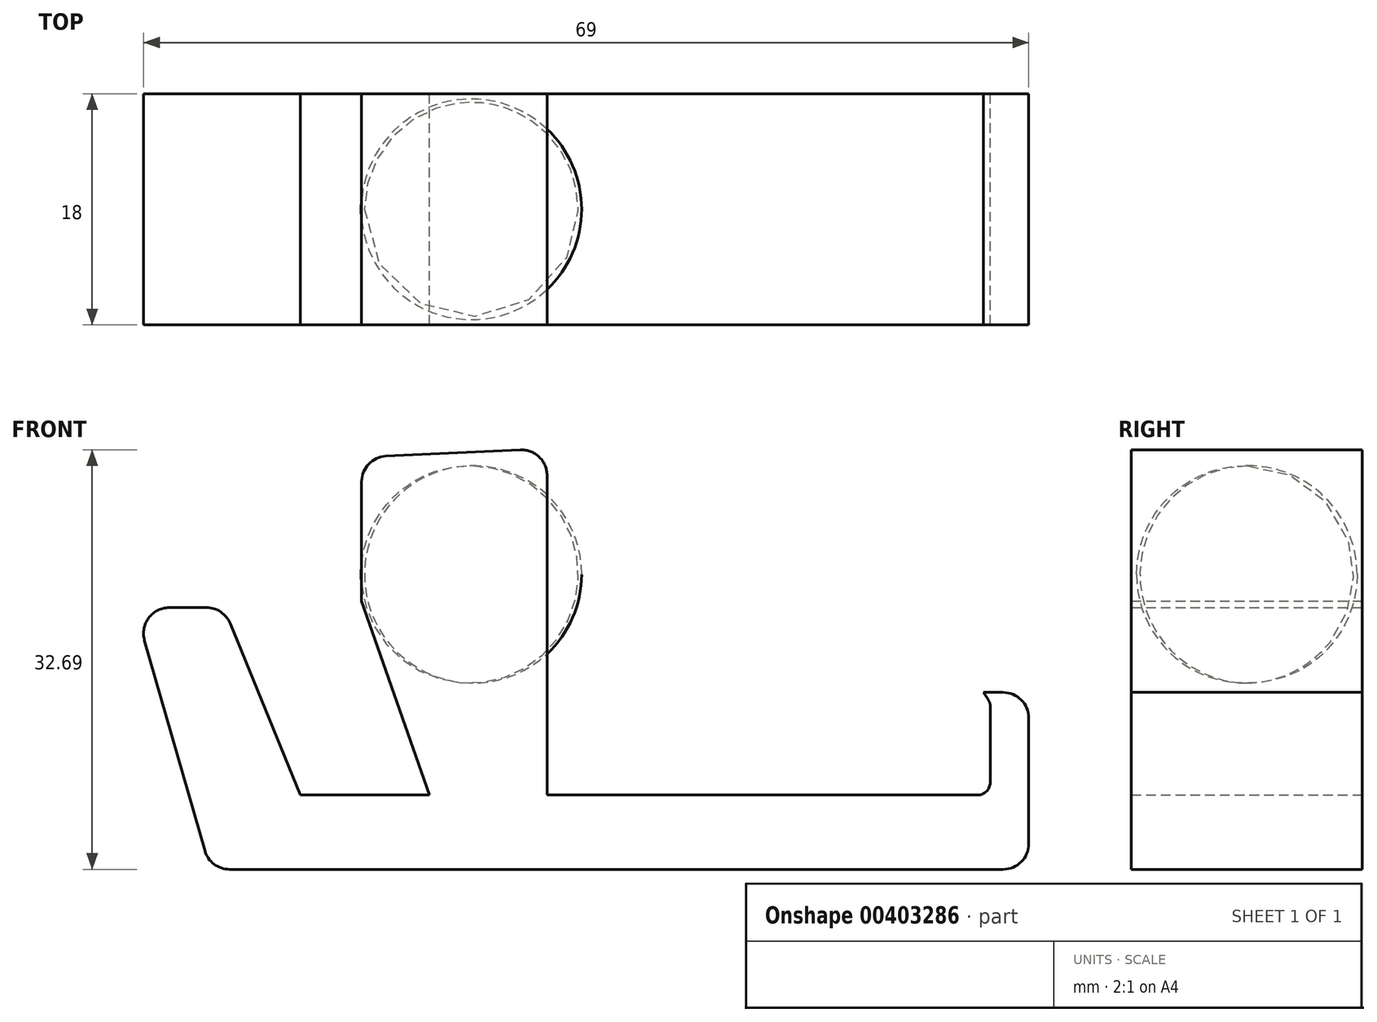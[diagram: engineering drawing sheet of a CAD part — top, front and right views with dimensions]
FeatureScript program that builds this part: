
annotation { "Feature Type Name" : "Feature", "Feature Type Description" : "" }
export const myFeature = defineFeature(function(context is Context, id is Id, definition is map)
    precondition{}
    {
        {
            var Q0;
            Q0=qCreatedBy(makeId("Front.planeOp"),FACE);
            var sketch = newSketch(context, id + "F0", { "sketchPlane" : qUnion([Q0])});
            skLineSegment(sketch, "E0", {"start": v(14.6, 13.8) * mm, "end": v(14.6, 0) * mm});
            skLineSegment(sketch, "E1", {"start": v(14.6, 0) * mm, "end": v(-21.99, 0) * mm});
            skLineSegment(sketch, "E2", {"start": v(-21.99, 0) * mm, "end": v(-49.2, 0) * mm});
            skLineSegment(sketch, "E3", {"start": v(-49.2, 0) * mm, "end": v(-55.06, 20.4) * mm});
            skLineSegment(sketch, "E4", {"start": v(-55.06, 20.4) * mm, "end": v(-48.16, 20.4) * mm});
            skLineSegment(sketch, "E5", {"start": v(-48.16, 20.4) * mm, "end": v(-42.19, 5.8) * mm});
            skLineSegment(sketch, "E6", {"start": v(-42.19, 5.8) * mm, "end": v(-32.13, 5.8) * mm});
            skLineSegment(sketch, "E7", {"start": v(-32.13, 5.8) * mm, "end": v(-37.4, 20.92) * mm});
            skLineSegment(sketch, "E8", {"start": v(-37.4, 20.92) * mm, "end": v(-37.4, 32.12) * mm});
            skLineSegment(sketch, "E9", {"start": v(-37.4, 32.12) * mm, "end": v(-22.95, 32.8) * mm});
            skLineSegment(sketch, "E10", {"start": v(-21.99, 0) * mm, "end": v(-21.99, 0) * mm});
            skLineSegment(sketch, "E11", {"start": v(-22.95, 5.8) * mm, "end": v(11.6, 5.8) * mm});
            skLineSegment(sketch, "E12", {"start": v(11.6, 5.8) * mm, "end": v(11.6, 13) * mm});
            skLineSegment(sketch, "E13", {"start": v(-22.95, 32.8) * mm, "end": v(-22.95, 5.8) * mm});
            skLineSegment(sketch, "E14", {"start": v(11.6, 13) * mm, "end": v(11.07, 13.8) * mm});
            skLineSegment(sketch, "E15", {"start": v(11.07, 13.8) * mm, "end": v(14.6, 13.8) * mm});
            skSolve(sketch);
        }
        {
            var Q0;
            Q0=makeQuery(id+"F0.imprint","IMPRINT",FACE,{"disambiguationData":[TD([[makeQuery(id+"F0.imprint","IMPRINT",EDGE,{"derivedFrom":sQuery(id+"F0.wireOp",EDGE,"E0")}),-1.0]])]});
            extrude(context, id + "F1", {"entities" : qUnion([Q0]), "depth" : 18 * mm});
        }
        {
            var Q0;
            Q0=makeQuery(id+"F1.opExtrude","SWEPT_EDGE",EDGE,{"disambiguationData":[OSD([sQuery(id+"F0.wireOp",EDGE,"E12"),sQuery(id+"F0.wireOp",EDGE,"p1Uv713Y-vDOA-6ysD-XTqa-nBpN6AyQfED6")])]});
            fillet(context, id + "F2", {"entities" : qUnion([Q0]), "radius" : 1 * mm, "tangentPropagation" : true, "allowEdgeOverflow" : false});
        }
        {
            var Q0;
            Q0=makeQuery(id+"F1.opExtrude","SWEPT_FACE",FACE,{"disambiguationData":[OSD([sQuery(id+"F0.wireOp",EDGE,"E13")])]});
            var sketch = newSketch(context, id + "F3", { "sketchPlane" : qUnion([Q0])});
            skCircle(sketch, "E16", {"center": v(-9.13, 22.98) * mm, "radius": 8.46 * mm});
            skLineSegment(sketch, "E17", {"start": v(-9, 32.8) * mm, "end": v(-9, 14.35) * mm});
            skSolve(sketch);
        }
        {
            var Q0;
            {var subQ0=sQuery(id+"F3.wireOp",EDGE,"E17");var subQ1=sQuery(id+"F3.wireOp",EDGE,"E16");var subQ2=makeQuery(id+"F3.imprint","INTERSECT",VERTEX,{"disambiguationData":[OD(0.0)],"derivedFrom":[subQ1,subQ0]});Q0=makeQuery(id+"F3.imprint","IMPRINT",FACE,{"disambiguationData":[TD([[makeQuery(id+"F3.imprint","IMPRINT",EDGE,{"disambiguationData":[TD([[subQ2,1.0]])],"derivedFrom":subQ1}),1.0]])]});}
            var Q1;
            Q1=sQuery(id+"F3.wireOp",EDGE,"E17");
            revolve(context, id + "F4", {"entities" : qUnion([Q0]), "axis" : qUnion([Q1]), "revolveType" : RevolveType.FULL});
        }
        {
            var Q0;
            Q0=makeQuery(id+"F1.opExtrude","SWEPT_BODY",BODY,{"disambiguationData":[OSD([sQuery(id+"F0.wireOp",EDGE,"E0"),sQuery(id+"F0.wireOp",EDGE,"E1"),sQuery(id+"F0.wireOp",EDGE,"E2"),sQuery(id+"F0.wireOp",EDGE,"E3"),sQuery(id+"F0.wireOp",EDGE,"E4"),sQuery(id+"F0.wireOp",EDGE,"E5"),sQuery(id+"F0.wireOp",EDGE,"E6"),sQuery(id+"F0.wireOp",EDGE,"E7"),sQuery(id+"F0.wireOp",EDGE,"E8"),sQuery(id+"F0.wireOp",EDGE,"E9"),sQuery(id+"F0.wireOp",EDGE,"E11"),sQuery(id+"F0.wireOp",EDGE,"E12"),sQuery(id+"F0.wireOp",EDGE,"E13"),sQuery(id+"F0.wireOp",EDGE,"E14"),sQuery(id+"F0.wireOp",EDGE,"3ds5d85f-Lgwv-mqfg-5s7Q-YuIEELG9T3Yo"),sQuery(id+"F0.wireOp",EDGE,"UHpZs6yJ-V90P-YT9Z-aao1-8wgQZAYxgrAd")])]});
            var Q1;
            Q1=makeQuery(id+"F4.opRevolve","SWEPT_FACE",FACE,{"disambiguationData":[OSD([sQuery(id+"F3.wireOp",EDGE,"E16")])]});
            transform(context, id + "F5", {"entities" : qUnion([Q0]), "transformType" : TransformType.TRANSLATION_3D, "dx" : 5.9 * mm, "dy" : 0 * mm, "dz" : 0 * mm, "makeCopy" : false});
        }
        {
            var Q0;
            Q0=makeQuery(id+"F1.opExtrude","SWEPT_EDGE",EDGE,{"disambiguationData":[OSD([sQuery(id+"F0.wireOp",EDGE,"E3"),sQuery(id+"F0.wireOp",EDGE,"E4")])]});
            var Q1;
            Q1=makeQuery(id+"F1.opExtrude","SWEPT_EDGE",EDGE,{"disambiguationData":[OSD([sQuery(id+"F0.wireOp",EDGE,"E2"),sQuery(id+"F0.wireOp",EDGE,"E3")])]});
            var Q2;
            Q2=makeQuery(id+"F1.opExtrude","SWEPT_EDGE",EDGE,{"disambiguationData":[OSD([sQuery(id+"F0.wireOp",EDGE,"E0"),sQuery(id+"F0.wireOp",EDGE,"E1")])]});
            var Q3;
            Q3=makeQuery(id+"F1.opExtrude","SWEPT_EDGE",EDGE,{"disambiguationData":[OSD([sQuery(id+"F0.wireOp",EDGE,"3ds5d85f-Lgwv-mqfg-5s7Q-YuIEELG9T3Yo"),sQuery(id+"F0.wireOp",EDGE,"UHpZs6yJ-V90P-YT9Z-aao1-8wgQZAYxgrAd")])]});
            var Q4;
            Q4=makeQuery(id+"F1.opExtrude","SWEPT_EDGE",EDGE,{"disambiguationData":[OSD([sQuery(id+"F0.wireOp",EDGE,"E9"),sQuery(id+"F0.wireOp",EDGE,"E13")])]});
            var Q5;
            Q5=makeQuery(id+"F1.opExtrude","SWEPT_EDGE",EDGE,{"disambiguationData":[OSD([sQuery(id+"F0.wireOp",EDGE,"E4"),sQuery(id+"F0.wireOp",EDGE,"E5")])]});
            var Q6;
            Q6=makeQuery(id+"F1.opExtrude","SWEPT_EDGE",EDGE,{"disambiguationData":[OSD([sQuery(id+"F0.wireOp",EDGE,"E8"),sQuery(id+"F0.wireOp",EDGE,"E9")])]});
            var Q7;
            Q7=makeQuery(id+"F1.opExtrude","SWEPT_EDGE",EDGE,{"disambiguationData":[OSD([sQuery(id+"F0.wireOp",EDGE,"E0"),sQuery(id+"F0.wireOp",EDGE,"E15")])]});
            fillet(context, id + "F6", {"entities" : qUnion([Q0, Q1, Q2, Q3, Q4, Q5, Q6, Q7]), "radius" : 2 * mm, "tangentPropagation" : true, "allowEdgeOverflow" : false});
        }
    });
